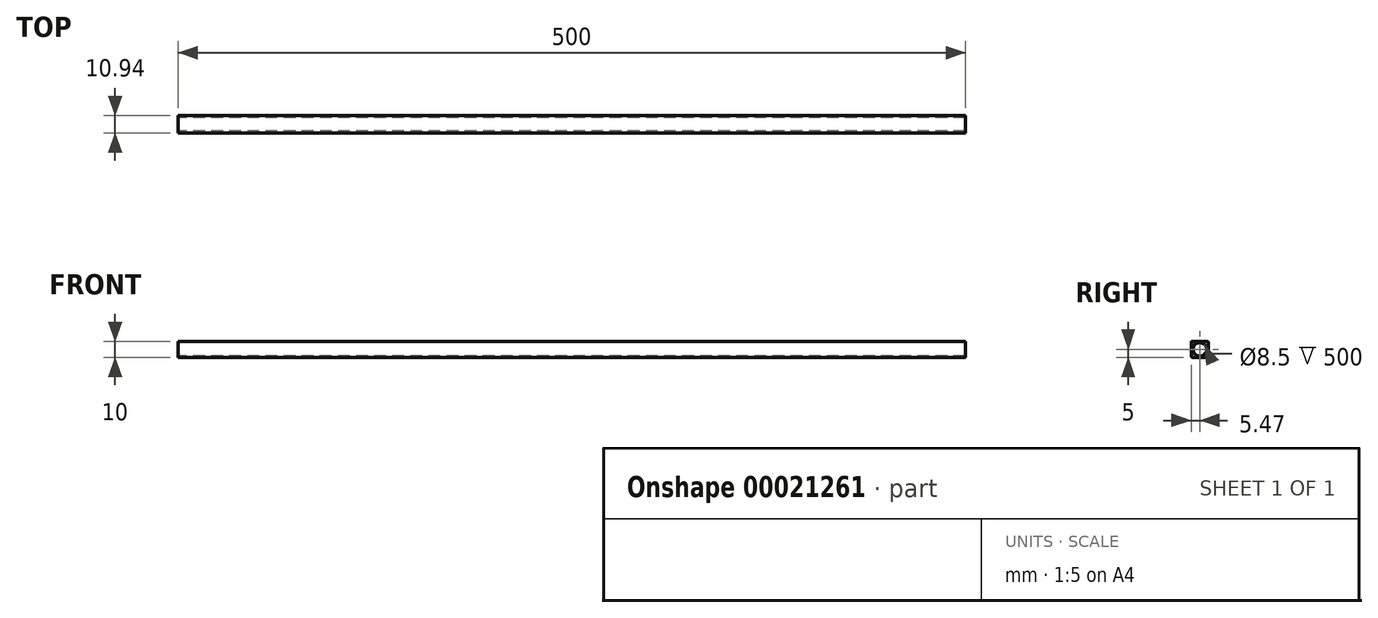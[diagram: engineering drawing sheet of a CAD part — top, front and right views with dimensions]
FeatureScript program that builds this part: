
annotation { "Feature Type Name" : "Feature", "Feature Type Description" : "" }
export const myFeature = defineFeature(function(context is Context, id is Id, definition is map)
    precondition{}
    {
        {
            var Q0;
            Q0=qCreatedBy(makeId("Right.planeOp"),FACE);
            var sketch = newSketch(context, id + "F0", { "sketchPlane" : qUnion([Q0])});
            skLineSegment(sketch, "E0.rect.bottom", {"start": v(4.97, -5) * mm, "end": v(-4.97, -5) * mm});
            skLineSegment(sketch, "E0.rect.top", {"start": v(4.97, 5) * mm, "end": v(-4.97, 5) * mm});
            skLineSegment(sketch, "E0.rect.left", {"start": v(5.47, -4.5) * mm, "end": v(5.47, 4.5) * mm});
            skLineSegment(sketch, "E0.rect.right", {"start": v(-5.47, -4.5) * mm, "end": v(-5.47, 4.5) * mm});
            skPoint(sketch, "E0.rect.middle", {"position": v(0, 0) * mm});
            skCircle(sketch, "E1", {"center": v(0, 0) * mm, "radius": 4.25 * mm});
            skPoint(sketch, "E2.visualSharp", {"position": v(-5.47, 5) * mm});
            skArc(sketch, "E2.filletArc", {"start": v(-4.97, 5) * mm, "mid": v(-5.32, 4.85) * mm, "end": v(-5.47, 4.5) * mm});
            skPoint(sketch, "E3.visualSharp", {"position": v(5.47, 5) * mm});
            skArc(sketch, "E3.filletArc", {"start": v(5.47, 4.5) * mm, "mid": v(5.32, 4.85) * mm, "end": v(4.97, 5) * mm});
            skPoint(sketch, "E4.visualSharp", {"position": v(5.47, -5) * mm});
            skArc(sketch, "E4.filletArc", {"start": v(4.97, -5) * mm, "mid": v(5.32, -4.85) * mm, "end": v(5.47, -4.5) * mm});
            skPoint(sketch, "E5.visualSharp", {"position": v(-5.47, -5) * mm});
            skArc(sketch, "E5.filletArc", {"start": v(-5.47, -4.5) * mm, "mid": v(-5.32, -4.85) * mm, "end": v(-4.97, -5) * mm});
            skSolve(sketch);
        }
        {
            var Q0;
            Q0 = qSketchRegion(id + "F0", true);
            extrude(context, id + "F1", {"entities" : qUnion([Q0]), "depth" : 500 * mm});
        }
    });
